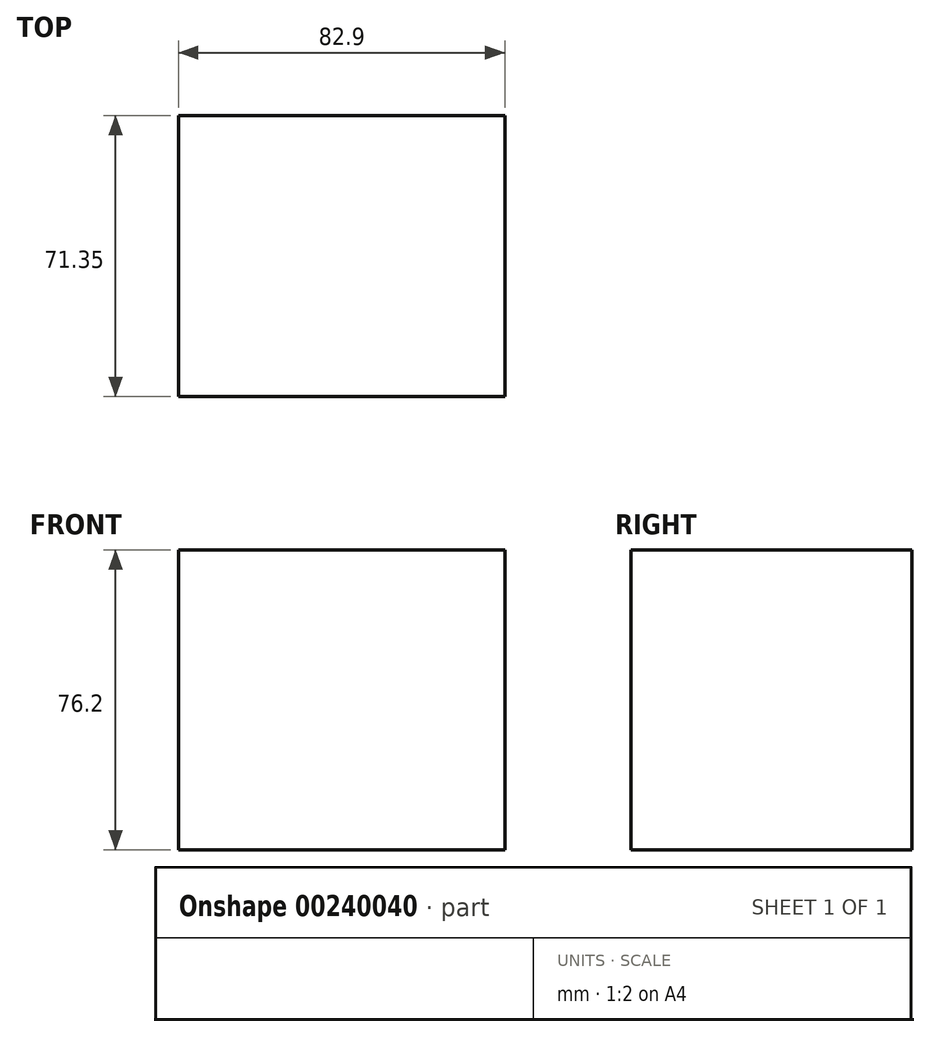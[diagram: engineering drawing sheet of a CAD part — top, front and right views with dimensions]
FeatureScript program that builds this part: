
annotation { "Feature Type Name" : "Feature", "Feature Type Description" : "" }
export const myFeature = defineFeature(function(context is Context, id is Id, definition is map)
    precondition{}
    {
        {
            var Q0;
            Q0=qCreatedBy(makeId("Top.planeOp"),FACE);
            var sketch = newSketch(context, id + "F0", { "sketchPlane" : qUnion([Q0])});
            skLineSegment(sketch, "E0.bottom", {"start": v(-40.64, 36.14) * mm, "end": v(42.26, 36.14) * mm});
            skLineSegment(sketch, "E0.top", {"start": v(-40.64, -35.21) * mm, "end": v(42.26, -35.21) * mm});
            skLineSegment(sketch, "E0.left", {"start": v(-40.64, 36.14) * mm, "end": v(-40.64, -35.21) * mm});
            skLineSegment(sketch, "E0.right", {"start": v(42.26, 36.14) * mm, "end": v(42.26, -35.21) * mm});
            skSolve(sketch);
        }
        {
            var Q0;
            Q0 = qSketchRegion(id + "F0", true);
            extrude(context, id + "F1", {"entities" : qUnion([Q0]), "depth" : 76.2 * mm});
        }
    });
